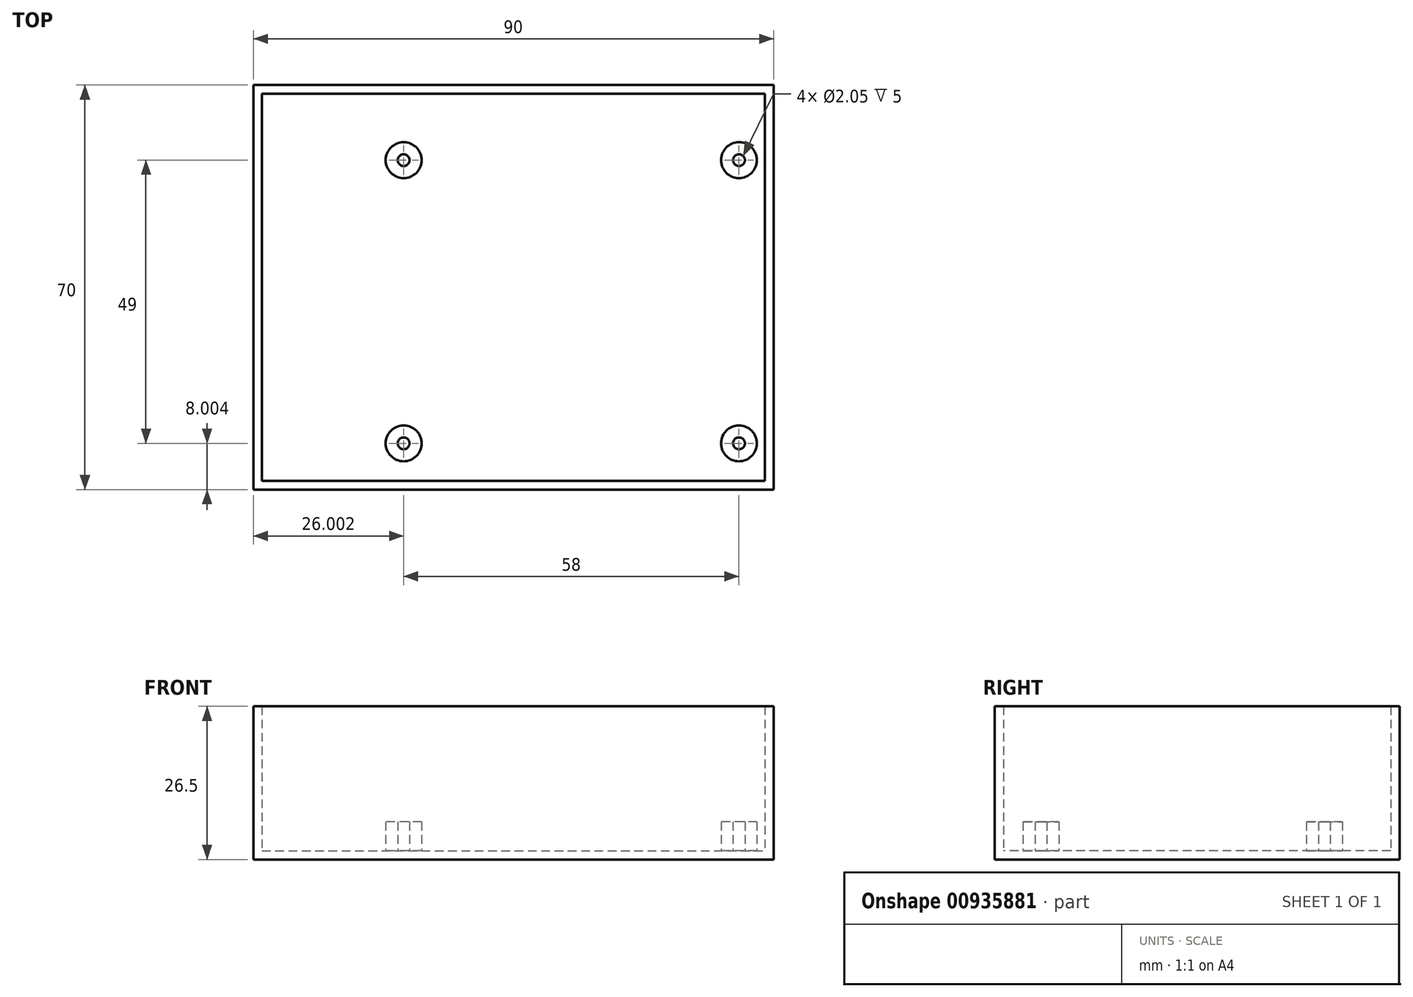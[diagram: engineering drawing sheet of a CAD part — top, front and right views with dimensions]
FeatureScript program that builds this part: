
annotation { "Feature Type Name" : "Feature", "Feature Type Description" : "" }
export const myFeature = defineFeature(function(context is Context, id is Id, definition is map)
    precondition{}
    {
        {
            var Q0;
            Q0=qCreatedBy(makeId("Top.planeOp"),FACE);
            var sketch = newSketch(context, id + "F0", { "sketchPlane" : qUnion([Q0])});
            skLineSegment(sketch, "E0.bottom", {"start": v(-45.8, 34.9) * mm, "end": v(44.2, 34.9) * mm});
            skLineSegment(sketch, "E0.top", {"start": v(-45.8, -35.1) * mm, "end": v(44.2, -35.1) * mm});
            skLineSegment(sketch, "E0.left", {"start": v(-45.8, 34.9) * mm, "end": v(-45.8, -35.1) * mm});
            skLineSegment(sketch, "E0.right", {"start": v(44.2, 34.9) * mm, "end": v(44.2, -35.1) * mm});
            skLineSegment(sketch, "E1.bottom", {"start": v(-44.3, 33.4) * mm, "end": v(42.7, 33.4) * mm});
            skLineSegment(sketch, "E1.top", {"start": v(-44.3, -33.6) * mm, "end": v(42.7, -33.6) * mm});
            skLineSegment(sketch, "E1.left", {"start": v(-44.3, 33.4) * mm, "end": v(-44.3, -33.6) * mm});
            skLineSegment(sketch, "E1.right", {"start": v(42.7, 33.4) * mm, "end": v(42.7, -33.6) * mm});
            skCircle(sketch, "E2", {"center": v(-19.8, 21.9) * mm, "radius": 3.1 * mm});
            skCircle(sketch, "E3", {"center": v(-19.8, -27.1) * mm, "radius": 3.1 * mm});
            skCircle(sketch, "E4", {"center": v(38.2, -27.1) * mm, "radius": 3.1 * mm});
            skCircle(sketch, "E5", {"center": v(38.2, 21.9) * mm, "radius": 3.1 * mm});
            skCircle(sketch, "E6", {"center": v(-19.8, 21.9) * mm, "radius": 1.02 * mm});
            skCircle(sketch, "E7", {"center": v(38.2, 21.9) * mm, "radius": 1.02 * mm});
            skCircle(sketch, "E8", {"center": v(38.2, -27.1) * mm, "radius": 1.02 * mm});
            skCircle(sketch, "E9", {"center": v(-19.8, -27.1) * mm, "radius": 1.02 * mm});
            skSolve(sketch);
        }
        {
            var Q0;
            Q0=makeQuery(id+"F0.imprint","IMPRINT",FACE,{"disambiguationData":[TD([[makeQuery(id+"F0.imprint","IMPRINT",EDGE,{"derivedFrom":sQuery(id+"F0.wireOp",EDGE,"E0.bottom")}),-1.0]])]});
            extrude(context, id + "F1", {"entities" : qUnion([Q0]), "depth" : 25 * mm, "offsetDistance" : 25 * mm});
        }
        {
            var Q0;
            Q0=makeQuery(id+"F0.imprint","IMPRINT",FACE,{"disambiguationData":[TD([[makeQuery(id+"F0.imprint","IMPRINT",EDGE,{"derivedFrom":sQuery(id+"F0.wireOp",EDGE,"E0.bottom")}),-1.0]])]});
            var Q1;
            Q1=makeQuery(id+"F0.imprint","IMPRINT",FACE,{"disambiguationData":[TD([[makeQuery(id+"F0.imprint","IMPRINT",EDGE,{"derivedFrom":sQuery(id+"F0.wireOp",EDGE,"E1.bottom")}),-1.0]])]});
            var Q2;
            Q2=makeQuery(id+"F0.imprint","IMPRINT",FACE,{"disambiguationData":[TD([[makeQuery(id+"F0.imprint","IMPRINT",EDGE,{"derivedFrom":sQuery(id+"F0.wireOp",EDGE,"E4")}),1.0]])]});
            var Q3;
            Q3=makeQuery(id+"F0.imprint","IMPRINT",FACE,{"disambiguationData":[TD([[makeQuery(id+"F0.imprint","IMPRINT",EDGE,{"derivedFrom":sQuery(id+"F0.wireOp",EDGE,"E8")}),1.0]])]});
            var Q4;
            Q4=makeQuery(id+"F0.imprint","IMPRINT",FACE,{"disambiguationData":[TD([[makeQuery(id+"F0.imprint","IMPRINT",EDGE,{"derivedFrom":sQuery(id+"F0.wireOp",EDGE,"E5")}),1.0]])]});
            var Q5;
            Q5=makeQuery(id+"F0.imprint","IMPRINT",FACE,{"disambiguationData":[TD([[makeQuery(id+"F0.imprint","IMPRINT",EDGE,{"derivedFrom":sQuery(id+"F0.wireOp",EDGE,"E7")}),1.0]])]});
            var Q6;
            Q6=makeQuery(id+"F0.imprint","IMPRINT",FACE,{"disambiguationData":[TD([[makeQuery(id+"F0.imprint","IMPRINT",EDGE,{"derivedFrom":sQuery(id+"F0.wireOp",EDGE,"E2")}),1.0]])]});
            var Q7;
            Q7=makeQuery(id+"F0.imprint","IMPRINT",FACE,{"disambiguationData":[TD([[makeQuery(id+"F0.imprint","IMPRINT",EDGE,{"derivedFrom":sQuery(id+"F0.wireOp",EDGE,"E6")}),1.0]])]});
            var Q8;
            Q8=makeQuery(id+"F0.imprint","IMPRINT",FACE,{"disambiguationData":[TD([[makeQuery(id+"F0.imprint","IMPRINT",EDGE,{"derivedFrom":sQuery(id+"F0.wireOp",EDGE,"E3")}),1.0]])]});
            var Q9;
            Q9=makeQuery(id+"F0.imprint","IMPRINT",FACE,{"disambiguationData":[TD([[makeQuery(id+"F0.imprint","IMPRINT",EDGE,{"derivedFrom":sQuery(id+"F0.wireOp",EDGE,"E9")}),1.0]])]});
            extrude(context, id + "F2", {"entities" : qUnion([Q0, Q1, Q2, Q3, Q4, Q5, Q6, Q7, Q8, Q9]), "operationType" : NewBodyOperationType.ADD, "oppositeDirection" : true, "depth" : 1.5 * mm, "offsetDistance" : 25 * mm});
        }
        {
            var Q0;
            Q0=makeQuery(id+"F0.imprint","IMPRINT",FACE,{"disambiguationData":[TD([[makeQuery(id+"F0.imprint","IMPRINT",EDGE,{"derivedFrom":sQuery(id+"F0.wireOp",EDGE,"E2")}),1.0]])]});
            var Q1;
            Q1=makeQuery(id+"F0.imprint","IMPRINT",FACE,{"disambiguationData":[TD([[makeQuery(id+"F0.imprint","IMPRINT",EDGE,{"derivedFrom":sQuery(id+"F0.wireOp",EDGE,"E5")}),1.0]])]});
            var Q2;
            Q2=makeQuery(id+"F0.imprint","IMPRINT",FACE,{"disambiguationData":[TD([[makeQuery(id+"F0.imprint","IMPRINT",EDGE,{"derivedFrom":sQuery(id+"F0.wireOp",EDGE,"E4")}),1.0]])]});
            var Q3;
            Q3=makeQuery(id+"F0.imprint","IMPRINT",FACE,{"disambiguationData":[TD([[makeQuery(id+"F0.imprint","IMPRINT",EDGE,{"derivedFrom":sQuery(id+"F0.wireOp",EDGE,"E3")}),1.0]])]});
            extrude(context, id + "F3", {"entities" : qUnion([Q0, Q1, Q2, Q3]), "operationType" : NewBodyOperationType.ADD, "depth" : 5 * mm, "offsetDistance" : 25 * mm});
        }
    });
